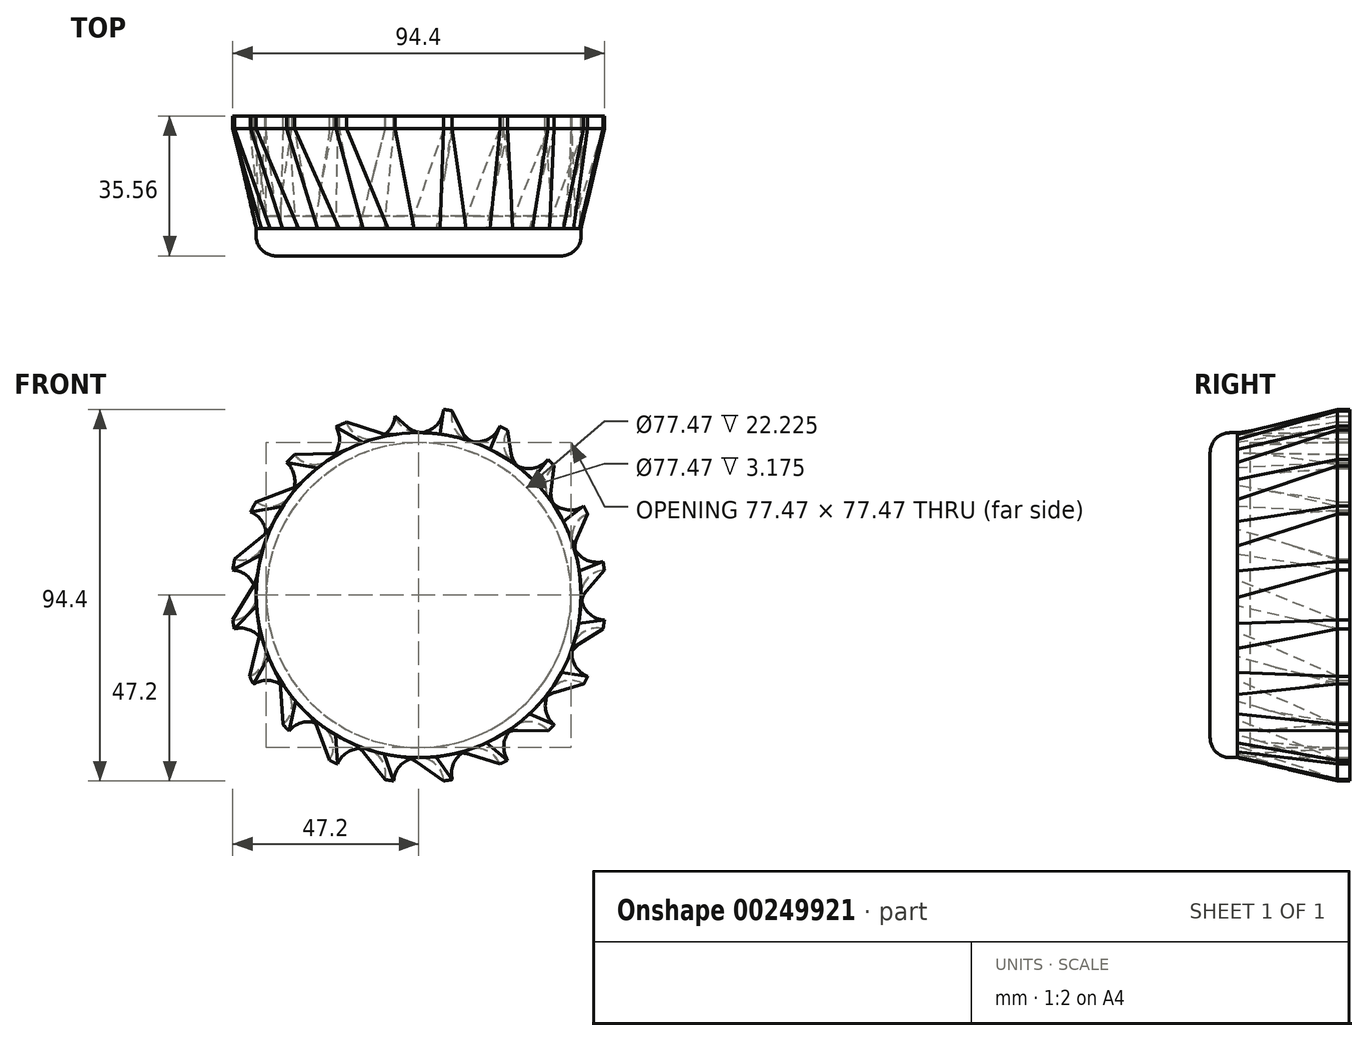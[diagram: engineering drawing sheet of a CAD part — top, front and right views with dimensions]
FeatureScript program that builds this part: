
annotation { "Feature Type Name" : "Feature", "Feature Type Description" : "" }
export const myFeature = defineFeature(function(context is Context, id is Id, definition is map)
    precondition{}
    {
        {
            var Q0;
            Q0=qCreatedBy(makeId("Front.planeOp"),FACE);
            var sketch = newSketch(context, id + "F0", { "sketchPlane" : qUnion([Q0])});
            skLineSegment(sketch, "E0", {"start": v(0, 61.32) * mm, "end": v(0, -70.45) * mm, "construction": true});
            skLineSegment(sketch, "E1", {"start": v(-64.98, 0) * mm, "end": v(71.22, 0) * mm, "construction": true});
            skCircle(sketch, "E2", {"center": v(0, 0) * mm, "radius": 47.63 * mm});
            skArc(sketch, "E3", {"start": v(-6.35, 47.2) * mm, "mid": v(0, 41.28) * mm, "end": v(6.35, 47.2) * mm});
            skArc(sketch, "E4.1.0", {"start": v(8.55, 46.85) * mm, "mid": v(12.75, 39.25) * mm, "end": v(20.62, 42.93) * mm});
            skArc(sketch, "E4.2.0", {"start": v(22.6, 41.92) * mm, "mid": v(24.26, 33.4) * mm, "end": v(32.88, 34.45) * mm});
            skArc(sketch, "E4.3.0", {"start": v(34.45, 32.88) * mm, "mid": v(33.4, 24.26) * mm, "end": v(41.92, 22.6) * mm});
            skArc(sketch, "E4.4.0", {"start": v(42.93, 20.62) * mm, "mid": v(39.25, 12.75) * mm, "end": v(46.85, 8.55) * mm});
            skArc(sketch, "E4.5.0", {"start": v(47.2, 6.35) * mm, "mid": v(41.28, 0) * mm, "end": v(47.2, -6.35) * mm});
            skCircle(sketch, "E4.5.1", {"center": v(0, 0) * mm, "radius": 41.28 * mm, "construction": true});
            skLineSegment(sketch, "E4.anchor1", {"start": v(0, 0) * mm, "end": v(-6.35, 47.2) * mm, "construction": true});
            skLineSegment(sketch, "E4.anchor2", {"start": v(0, 0) * mm, "end": v(47.2, 6.35) * mm, "construction": true});
            skArc(sketch, "E5.1.0", {"start": v(46.85, -8.55) * mm, "mid": v(39.25, -12.75) * mm, "end": v(42.93, -20.62) * mm});
            skArc(sketch, "E5.2.0", {"start": v(41.92, -22.6) * mm, "mid": v(33.4, -24.26) * mm, "end": v(34.45, -32.88) * mm});
            skArc(sketch, "E5.3.0", {"start": v(32.88, -34.45) * mm, "mid": v(24.26, -33.4) * mm, "end": v(22.6, -41.92) * mm});
            skArc(sketch, "E5.4.0", {"start": v(20.62, -42.93) * mm, "mid": v(12.75, -39.25) * mm, "end": v(8.55, -46.85) * mm});
            skArc(sketch, "E5.5.0", {"start": v(6.35, -47.2) * mm, "mid": v(0, -41.28) * mm, "end": v(-6.35, -47.2) * mm});
            skLineSegment(sketch, "E5.anchor1", {"start": v(0, 0) * mm, "end": v(47.2, -6.35) * mm, "construction": true});
            skLineSegment(sketch, "E5.anchor2", {"start": v(0, 0) * mm, "end": v(-6.35, -47.2) * mm, "construction": true});
            skArc(sketch, "E6.1.0", {"start": v(-8.55, -46.85) * mm, "mid": v(-12.75, -39.25) * mm, "end": v(-20.62, -42.93) * mm});
            skArc(sketch, "E6.2.0", {"start": v(-22.6, -41.92) * mm, "mid": v(-24.26, -33.4) * mm, "end": v(-32.88, -34.45) * mm});
            skArc(sketch, "E6.3.0", {"start": v(-34.45, -32.88) * mm, "mid": v(-33.4, -24.26) * mm, "end": v(-41.92, -22.6) * mm});
            skArc(sketch, "E6.4.0", {"start": v(-42.93, -20.62) * mm, "mid": v(-39.25, -12.75) * mm, "end": v(-46.85, -8.55) * mm});
            skArc(sketch, "E6.5.0", {"start": v(-47.2, -6.35) * mm, "mid": v(-41.28, 0) * mm, "end": v(-47.2, 6.35) * mm});
            skLineSegment(sketch, "E6.anchor2", {"start": v(0, 0) * mm, "end": v(-47.2, 6.35) * mm, "construction": true});
            skArc(sketch, "E7.1.0", {"start": v(-46.74, 9.16) * mm, "mid": v(-39.08, 13.27) * mm, "end": v(-42.65, 21.18) * mm});
            skArc(sketch, "E7.2.0", {"start": v(-41.31, 23.7) * mm, "mid": v(-32.75, 25.13) * mm, "end": v(-33.58, 33.77) * mm});
            skArc(sketch, "E7.3.0", {"start": v(-31.5, 35.72) * mm, "mid": v(-22.93, 34.32) * mm, "end": v(-20.94, 42.77) * mm});
            skArc(sketch, "E7.4.0", {"start": v(-18.35, 43.95) * mm, "mid": v(-10.68, 39.87) * mm, "end": v(-6.08, 47.23) * mm});
            skLineSegment(sketch, "E7.anchor1", {"start": v(0, 0) * mm, "end": v(-47.2, -6.35) * mm, "construction": true});
            skLineSegment(sketch, "E7.anchor2", {"start": v(0, 0) * mm, "end": v(-18.35, 43.95) * mm, "construction": true});
            skSolve(sketch);
        }
        {
            var Q0;
            {var subQ17=sQuery(id+"F0.wireOp",EDGE,"E4.1.0");Q0=makeQuery(id+"F0.imprint","IMPRINT",FACE,{"disambiguationData":[TD([[makeQuery(id+"F0.imprint","IMPRINT",EDGE,{"derivedFrom":subQ17}),-1.0]])]});}
            extrude(context, id + "F1", {"entities" : qUnion([Q0]), "depth" : 3.17 * mm});
        }
        {
            var Q0;
            Q0=makeQuery(id+"F1.opExtrude","CAP_FACE",FACE,{"disambiguationData":[OSD([sQuery(id+"F0.wireOp",EDGE,"E2"),sQuery(id+"F0.wireOp",EDGE,"E3"),sQuery(id+"F0.wireOp",EDGE,"E4.1.0"),sQuery(id+"F0.wireOp",EDGE,"E4.2.0"),sQuery(id+"F0.wireOp",EDGE,"E4.3.0"),sQuery(id+"F0.wireOp",EDGE,"E4.4.0"),sQuery(id+"F0.wireOp",EDGE,"E4.5.0"),sQuery(id+"F0.wireOp",EDGE,"E5.1.0"),sQuery(id+"F0.wireOp",EDGE,"E5.2.0"),sQuery(id+"F0.wireOp",EDGE,"E5.3.0"),sQuery(id+"F0.wireOp",EDGE,"E5.4.0"),sQuery(id+"F0.wireOp",EDGE,"E5.5.0"),sQuery(id+"F0.wireOp",EDGE,"E6.1.0"),sQuery(id+"F0.wireOp",EDGE,"E6.2.0"),sQuery(id+"F0.wireOp",EDGE,"E6.3.0"),sQuery(id+"F0.wireOp",EDGE,"E6.4.0"),sQuery(id+"F0.wireOp",EDGE,"E6.5.0"),sQuery(id+"F0.wireOp",EDGE,"E7.1.0"),sQuery(id+"F0.wireOp",EDGE,"E7.2.0"),sQuery(id+"F0.wireOp",EDGE,"E7.3.0"),sQuery(id+"F0.wireOp",EDGE,"E7.4.0")])],"isStart":false});
            cPlane(context, id + "F2", {"entities" : qUnion([Q0]), "cplaneType" : CPlaneType.OFFSET, "offset" : 25.4 * mm, "width" : 152.4 * mm, "height" : 152.4 * mm});
        }
        {
            var Q0;
            Q0=qCreatedBy(id+"F2.planeOp",FACE);
            var sketch = newSketch(context, id + "F3", { "sketchPlane" : qUnion([Q0])});
            skCircle(sketch, "E8", {"center": v(0, 0) * mm, "radius": 41.28 * mm});
            skSolve(sketch);
        }
        {
            var Q0;
            Q0=makeQuery(id+"F3.imprint","IMPRINT",FACE,{"disambiguationData":[TD([[makeQuery(id+"F3.imprint","IMPRINT",EDGE,{"derivedFrom":sQuery(id+"F3.wireOp",EDGE,"E8")}),1.0]])]});
            extrude(context, id + "F4", {"entities" : qUnion([Q0]), "depth" : 7 * mm});
        }
        {
            var Q0;
            Q0=makeQuery(id+"F1.opExtrude","CAP_FACE",FACE,{"disambiguationData":[OSD([sQuery(id+"F0.wireOp",EDGE,"E2"),sQuery(id+"F0.wireOp",EDGE,"E3"),sQuery(id+"F0.wireOp",EDGE,"E4.1.0"),sQuery(id+"F0.wireOp",EDGE,"E4.2.0"),sQuery(id+"F0.wireOp",EDGE,"E4.3.0"),sQuery(id+"F0.wireOp",EDGE,"E4.4.0"),sQuery(id+"F0.wireOp",EDGE,"E4.5.0"),sQuery(id+"F0.wireOp",EDGE,"E5.1.0"),sQuery(id+"F0.wireOp",EDGE,"E5.2.0"),sQuery(id+"F0.wireOp",EDGE,"E5.3.0"),sQuery(id+"F0.wireOp",EDGE,"E5.4.0"),sQuery(id+"F0.wireOp",EDGE,"E5.5.0"),sQuery(id+"F0.wireOp",EDGE,"E6.1.0"),sQuery(id+"F0.wireOp",EDGE,"E6.2.0"),sQuery(id+"F0.wireOp",EDGE,"E6.3.0"),sQuery(id+"F0.wireOp",EDGE,"E6.4.0"),sQuery(id+"F0.wireOp",EDGE,"E6.5.0"),sQuery(id+"F0.wireOp",EDGE,"E7.1.0"),sQuery(id+"F0.wireOp",EDGE,"E7.2.0"),sQuery(id+"F0.wireOp",EDGE,"E7.3.0"),sQuery(id+"F0.wireOp",EDGE,"E7.4.0")])],"isStart":false});
            var Q1;
            Q1=makeQuery(id+"F4.opExtrude","CAP_FACE",FACE,{"disambiguationData":[OSD([sQuery(id+"F3.wireOp",EDGE,"E8")])],"isStart":true});
            loft(context, id + "F5", {"sheetProfilesArray" : [{ "sheetProfileEntities" : qUnion([Q0]) }, { "sheetProfileEntities" : qUnion([Q1]) }]});
        }
        {
            var Q0;
            Q0=makeQuery(id+"F1.opExtrude","CAP_FACE",FACE,{"disambiguationData":[OSD([sQuery(id+"F0.wireOp",EDGE,"E2"),sQuery(id+"F0.wireOp",EDGE,"E3"),sQuery(id+"F0.wireOp",EDGE,"E4.1.0"),sQuery(id+"F0.wireOp",EDGE,"E4.2.0"),sQuery(id+"F0.wireOp",EDGE,"E4.3.0"),sQuery(id+"F0.wireOp",EDGE,"E4.4.0"),sQuery(id+"F0.wireOp",EDGE,"E4.5.0"),sQuery(id+"F0.wireOp",EDGE,"E5.1.0"),sQuery(id+"F0.wireOp",EDGE,"E5.2.0"),sQuery(id+"F0.wireOp",EDGE,"E5.3.0"),sQuery(id+"F0.wireOp",EDGE,"E5.4.0"),sQuery(id+"F0.wireOp",EDGE,"E5.5.0"),sQuery(id+"F0.wireOp",EDGE,"E6.1.0"),sQuery(id+"F0.wireOp",EDGE,"E6.2.0"),sQuery(id+"F0.wireOp",EDGE,"E6.3.0"),sQuery(id+"F0.wireOp",EDGE,"E6.4.0"),sQuery(id+"F0.wireOp",EDGE,"E6.5.0"),sQuery(id+"F0.wireOp",EDGE,"E7.1.0"),sQuery(id+"F0.wireOp",EDGE,"E7.2.0"),sQuery(id+"F0.wireOp",EDGE,"E7.3.0"),sQuery(id+"F0.wireOp",EDGE,"E7.4.0")])],"isStart":true});
            var sketch = newSketch(context, id + "F6", { "sketchPlane" : qUnion([Q0])});
            skCircle(sketch, "E9", {"center": v(0, 0) * mm, "radius": 38.73 * mm});
            skSolve(sketch);
        }
        {
            var Q0;
            Q0=makeQuery(id+"F6.imprint","IMPRINT",FACE,{"disambiguationData":[TD([[makeQuery(id+"F6.imprint","IMPRINT",EDGE,{"derivedFrom":sQuery(id+"F6.wireOp",EDGE,"E9")}),1.0]])]});
            extrude(context, id + "F7", {"entities" : qUnion([Q0]), "operationType" : NewBodyOperationType.REMOVE, "oppositeDirection" : true, "depth" : 25.4 * mm});
        }
        {
            var Q0;
            Q0=makeQuery(id+"F4.opExtrude","CAP_EDGE",EDGE,{"disambiguationData":[OSD([sQuery(id+"F3.wireOp",EDGE,"E8")])],"isStart":false});
            fillet(context, id + "F8", {"entities" : qUnion([Q0]), "radius" : 5.08 * mm, "tangentPropagation" : true, "allowEdgeOverflow" : false});
        }
    });
